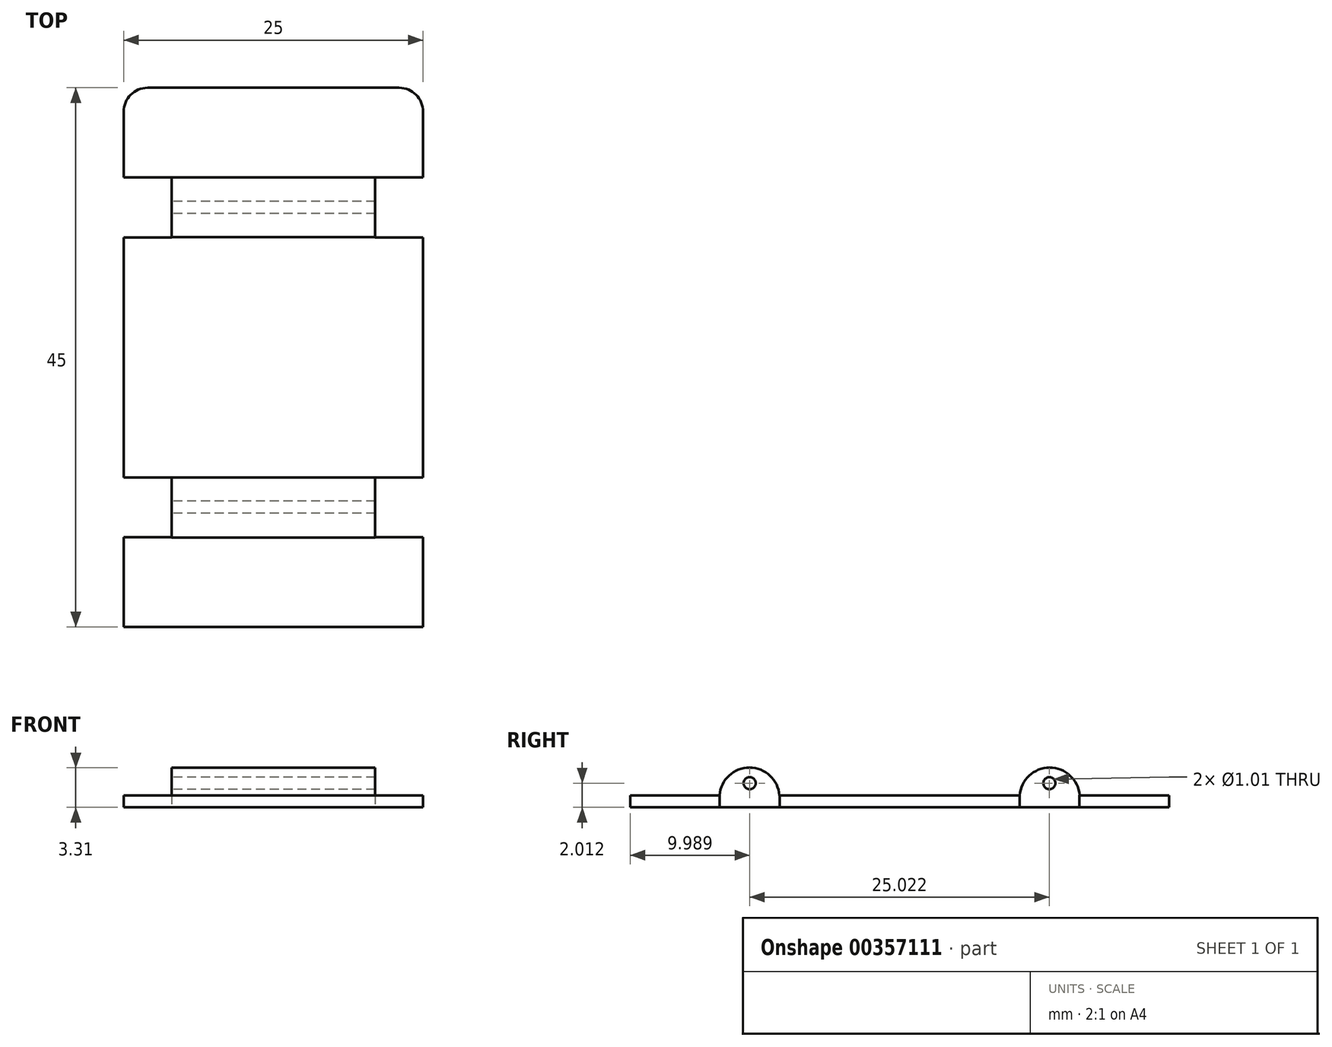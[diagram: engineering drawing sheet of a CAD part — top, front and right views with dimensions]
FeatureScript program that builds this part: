
annotation { "Feature Type Name" : "Feature", "Feature Type Description" : "" }
export const myFeature = defineFeature(function(context is Context, id is Id, definition is map)
    precondition{}
    {
        {
            var Q0;
            Q0=qCreatedBy(makeId("Top.planeOp"),FACE);
            var sketch = newSketch(context, id + "F0", { "sketchPlane" : qUnion([Q0])});
            skLineSegment(sketch, "E0.bottom", {"start": v(12.5, -22.5) * mm, "end": v(-12.5, -22.5) * mm});
            skLineSegment(sketch, "E0.top", {"start": v(10.5, 22.5) * mm, "end": v(-10.5, 22.5) * mm});
            skLineSegment(sketch, "E0.left", {"start": v(12.5, -22.5) * mm, "end": v(12.5, -15.02) * mm});
            skLineSegment(sketch, "E0.right", {"start": v(-12.5, -22.5) * mm, "end": v(-12.5, -15.02) * mm});
            skPoint(sketch, "E0.middle", {"position": v(0, 0) * mm});
            skLineSegment(sketch, "E1.bottom", {"start": v(-12.5, 15.02) * mm, "end": v(-8.5, 15.02) * mm});
            skLineSegment(sketch, "E1.top", {"start": v(-12.5, 10.02) * mm, "end": v(-8.5, 10.02) * mm});
            skLineSegment(sketch, "E1.right", {"start": v(-8.5, 15.02) * mm, "end": v(-8.5, 10.02) * mm});
            skLineSegment(sketch, "E2.MirrorCS", {"start": v(12.5, 15.02) * mm, "end": v(8.5, 15.02) * mm});
            skLineSegment(sketch, "E3.MirrorCS", {"start": v(8.5, 15.02) * mm, "end": v(8.5, 10.02) * mm});
            skLineSegment(sketch, "E4.MirrorCS", {"start": v(12.5, 10.02) * mm, "end": v(8.5, 10.02) * mm});
            skLineSegment(sketch, "E5.MirrorCS", {"start": v(12.5, -15.02) * mm, "end": v(8.5, -15.02) * mm});
            skLineSegment(sketch, "E6.MirrorCS", {"start": v(8.5, -15.02) * mm, "end": v(8.5, -10.02) * mm});
            skLineSegment(sketch, "E7.MirrorCS", {"start": v(12.5, -10.02) * mm, "end": v(8.5, -10.02) * mm});
            skLineSegment(sketch, "E8.MirrorCS", {"start": v(-12.5, -15.02) * mm, "end": v(-8.5, -15.02) * mm});
            skLineSegment(sketch, "E9.MirrorCS", {"start": v(-8.5, -15.02) * mm, "end": v(-8.5, -10.02) * mm});
            skLineSegment(sketch, "E10.MirrorCS", {"start": v(-12.5, -10.02) * mm, "end": v(-8.5, -10.02) * mm});
            skLineSegment(sketch, "E11.trimOffspring", {"start": v(-12.5, 15.02) * mm, "end": v(-12.5, 20.5) * mm});
            skLineSegment(sketch, "E12.trimOffspring", {"start": v(12.5, 15.02) * mm, "end": v(12.5, 20.5) * mm});
            skLineSegment(sketch, "E13.trimOffspring", {"start": v(12.5, -10.02) * mm, "end": v(12.5, 10.02) * mm});
            skLineSegment(sketch, "E14.trimOffspring", {"start": v(-12.5, -10.02) * mm, "end": v(-12.5, 10.02) * mm});
            skPoint(sketch, "E15.visualSharp", {"position": v(-12.5, 22.5) * mm});
            skArc(sketch, "E15.filletArc", {"start": v(-10.5, 22.5) * mm, "mid": v(-11.91, 21.91) * mm, "end": v(-12.5, 20.5) * mm});
            skPoint(sketch, "E16.visualSharp", {"position": v(12.5, 22.5) * mm});
            skArc(sketch, "E16.filletArc", {"start": v(12.5, 20.5) * mm, "mid": v(11.91, 21.91) * mm, "end": v(10.5, 22.5) * mm});
            skSolve(sketch);
        }
        {
            var Q0;
            Q0 = qSketchRegion(id + "F0", true);
            extrude(context, id + "F1", {"entities" : qUnion([Q0]), "depth" : 1 * mm});
        }
        {
            var Q0;
            Q0=qCreatedBy(makeId("Right.planeOp"),FACE);
            var sketch = newSketch(context, id + "F2", { "sketchPlane" : qUnion([Q0])});
            skArc(sketch, "E17", {"start": v(-10.03, 1) * mm, "mid": v(-12.52, 3.31) * mm, "end": v(-15.03, 1) * mm});
            skLineSegment(sketch, "E18", {"start": v(-15.03, 1) * mm, "end": v(-10.03, 1) * mm});
            skCircle(sketch, "E19", {"center": v(-12.51, 2.01) * mm, "radius": 0.5 * mm});
            skArc(sketch, "E20.MirrorCS", {"start": v(10.03, 1) * mm, "mid": v(12.52, 3.31) * mm, "end": v(15.03, 1) * mm});
            skCircle(sketch, "E21.MirrorC", {"center": v(12.51, 2.01) * mm, "radius": 0.5 * mm});
            skLineSegment(sketch, "E22.MirrorCS", {"start": v(15.03, 1) * mm, "end": v(10.03, 1) * mm});
            skSolve(sketch);
        }
        {
            var Q0;
            Q0 = qSketchRegion(id + "F2", true);
            extrude(context, id + "F3", {"entities" : qUnion([Q0]), "operationType" : NewBodyOperationType.ADD, "endBound" : BoundingType.SYMMETRIC, "depth" : 17 * mm});
        }
    });
